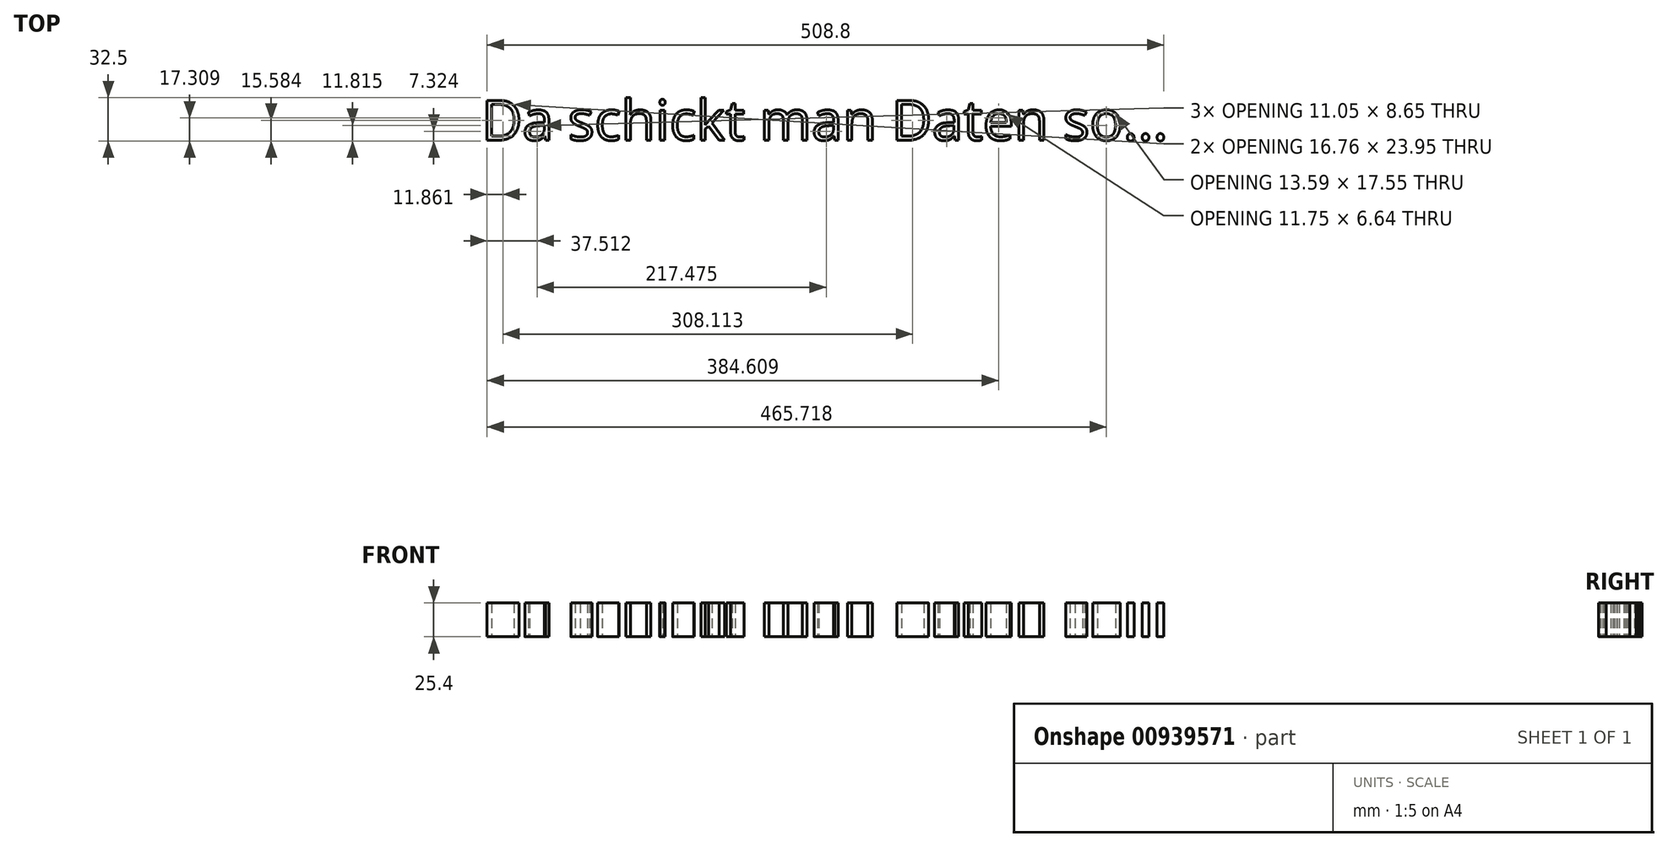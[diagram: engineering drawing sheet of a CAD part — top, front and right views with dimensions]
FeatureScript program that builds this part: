
annotation { "Feature Type Name" : "Feature", "Feature Type Description" : "" }
export const myFeature = defineFeature(function(context is Context, id is Id, definition is map)
    precondition{}
    {
        {
            var Q0;
            Q0=qCreatedBy(makeId("Top.planeOp"),FACE);
            var sketch = newSketch(context, id + "F0", { "sketchPlane" : qUnion([Q0])});
            skText(sketch, "E0", { "text": "Da schickt man Daten so...", "fontName": "OpenSans-Regular.ttf"});
            const initialGuessF0  = {"E0": [-0.20455, -0.06639, 1, 0, 0.03023]};
            skSetInitialGuess(sketch, initialGuessF0);
            skSolve(sketch);
        }
        {
            var Q0;
            Q0 = qSketchRegion(id + "F0", true);
            extrude(context, id + "F1", {"entities" : qUnion([Q0]), "depth" : 25.4 * mm, "offsetDistance" : 25.4 * mm});
        }
    });
